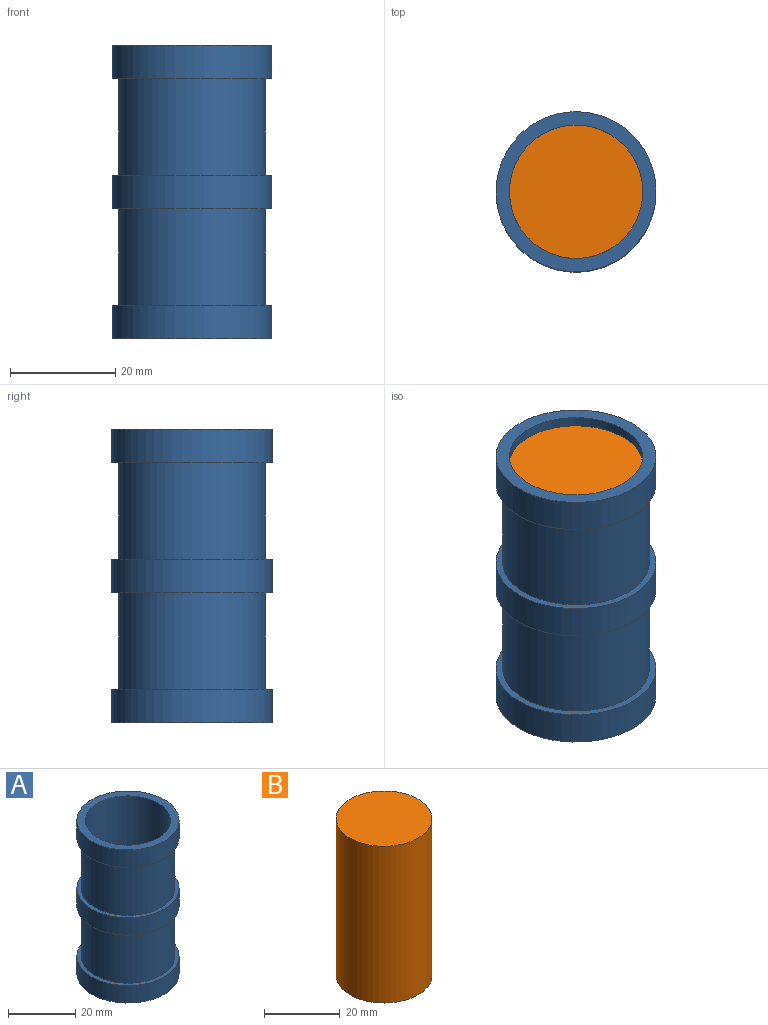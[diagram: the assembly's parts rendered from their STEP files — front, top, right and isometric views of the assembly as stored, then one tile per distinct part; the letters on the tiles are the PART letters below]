
ASSEMBLY  parts=2 mates=1
PART A: 13 faces, bbox 30.5x30.5x55.9 mm
  f0: cylinder r=12.7mm len=52.71mm, axis (0,0,-1), area 4205.7mm2, adj f1,f12
  f1: plane 25.4x25.4mm, normal (0,0,1), area 506.7mm2, adj f0
  f2: plane 30.48x30.48mm, normal (0,0,-1), area 729.7mm2, adj f3
  f3: cylinder r=15.24mm len=30.48mm, axis (0,0,-1), area 608mm2, adj f2,f4
  f4: plane 30.48x30.48mm, normal (0,0,1), area 116.5mm2, adj f3,f5
  f5: cylinder r=13.97mm len=27.94mm, axis (0,0,-1), area 1616.4mm2, adj f4,f6
  f6: plane 30.48x30.48mm, normal (0,0,-1), area 116.5mm2, adj f5,f7
  f7: cylinder r=15.24mm len=30.48mm, axis (0,0,-1), area 608mm2, adj f6,f8
  f8: plane 30.48x30.48mm, normal (0,0,1), area 116.5mm2, adj f7,f9
  f9: cylinder r=13.97mm len=27.94mm, axis (0,0,-1), area 1616.4mm2, adj f8,f10
  f10: plane 30.48x30.48mm, normal (0,0,-1), area 116.5mm2, adj f9,f11
  f11: cylinder r=15.24mm len=30.48mm, axis (0,0,-1), area 608mm2, adj f10,f12
  f12: plane 30.48x30.48mm, normal (0,0,1), area 223mm2, adj f0,f11
PART B: 3 faces, bbox 25.4x25.4x50.8 mm
  f0: cylinder r=12.7mm len=50.8mm, axis (0,0,-1), area 4053.7mm2, adj f1,f2
  f1: plane 25.4x25.4mm, normal (0,0,1), area 506.7mm2, adj f0
  f2: plane 25.4x25.4mm, normal (0,0,-1), area 506.7mm2, adj f0
PLACE A t=(7.27,20.24,-1.62)mm
PLACE B t=(7.27,20.24,1.56)mm
MATE fastened A.f0 <-> B.f0  axis (0,0,1) through (7.27,20.24,1.56)mm
